# Revit family: IS_Mara_Multiproduct_BIM_FR_A9025;A9026
name_source: partatom
category: Plumbing Fixtures
revit_build: Autodesk Revit MEP 2016 (Build: 20161004_0715(x64)
units: mm (PartAtom-declared; Revit-internal decimal feet)

## family parameters
Cut with Voids When Loaded = No
Host = Face
OmniClass Number = 23.45.55.17
OmniClass Title = Mixing Faucets
Part Type = Normal
Room Calculation Point = No
Round Connector Dimension = Use Diameter
Shared = Yes

## types (2) — shared parameters
Accessoires = www.idealspec.fr
Assembly Code = C1030200
Bim-NomDuProjet = ISI_IdealStandard_Mara_A9025_A9026
Conformité = NF
ConseilsDInstallation = 0
DateDeCréation = 43351
Default Elevation = 800 mm  [stored 2.62467 ft]
Dimensions = 181 x 163 x 74 mm
Espace = Interne
Forme = Complexe
Hauteur = 181 mm  [stored 0.593832 ft]
InformationsProduit = www.idealspec.fr
Largeur = 163 mm  [stored 0.534777 ft]
Longueur = 74 mm  [stored 0.242782 ft]
Marque = Ideal Standard
NBSDescription = Shower mixers
NBSReference = 45-35-70/335
PoidsNet = 0
Raccordement = Plomberie
Révision = 1
URL = www.idealspec.fr
Uniclass2015Code = Pr_40_20_87_75
Uniclass2015Title = Shower fittings package
UnitéDeMesure = Millimètres
UnitéDeTemps = An
UnitéMonétaire = €
UrlDuFabricant = www.idealspec.fr
zero-valued in all types: CWFU, Cost, CoûtDeRemplacement, HWFU, Profondeur, WFU

## per-type parameters (varying)
| type | A9025 | Caractéristiques | Description | Model |
| A9025AA - MARA BSH MXR B-IN KIT2 CHROME EASY-BOX | Yes | Kit Easy Box Avec Inverseur | Kit Easy Box Avec Inverseur | A9025GN |
| A9026AA - MARA SHR MXR B-IN KIT2 CHROME EASY-BOX | No | Kit Easy Boxsans Inverseur | Kit Easy Boxsans Inverseur | A9026GN |

note: [stored X ft] marks values corroborated as IEEE doubles in the binary element streams (Revit-internal decimal feet)

## geometry (parser evidence)
native form markers: Blend x4, Sweep x1
no freeform markers — native parametric forms only
